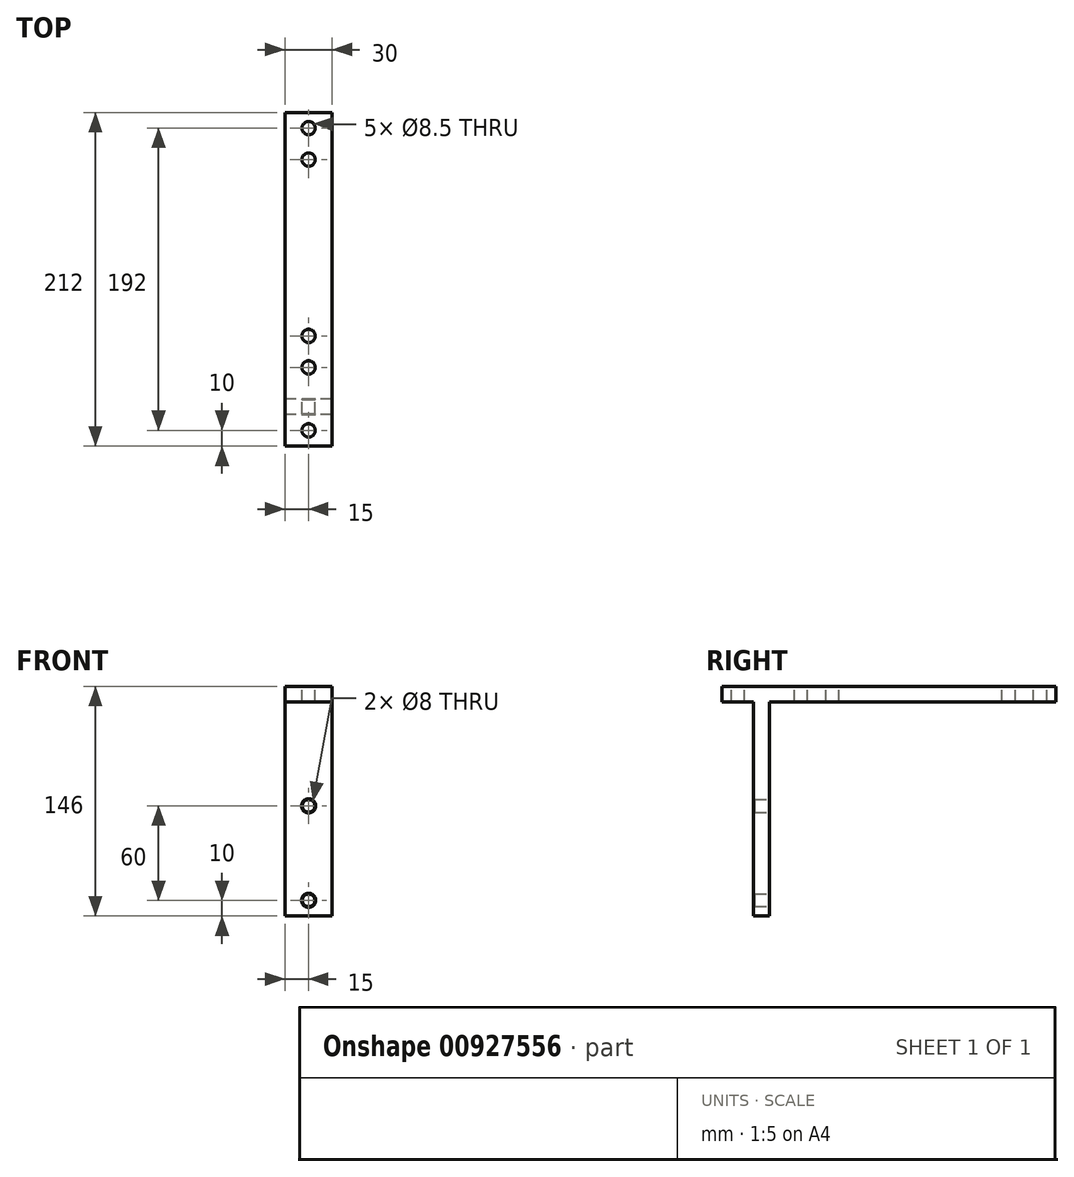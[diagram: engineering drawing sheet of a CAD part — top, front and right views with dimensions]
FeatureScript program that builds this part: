
annotation { "Feature Type Name" : "Feature", "Feature Type Description" : "" }
export const myFeature = defineFeature(function(context is Context, id is Id, definition is map)
    precondition{}
    {
        {
            var Q0;
            Q0=qCreatedBy(makeId("Right.planeOp"),FACE);
            var sketch = newSketch(context, id + "F0", { "sketchPlane" : qUnion([Q0])});
            skLineSegment(sketch, "E0", {"start": v(10, 136) * mm, "end": v(192, 136) * mm});
            skLineSegment(sketch, "E1", {"start": v(10, 136) * mm, "end": v(10, 0) * mm});
            skLineSegment(sketch, "E2.0", {"start": v(0, 146) * mm, "end": v(192, 146) * mm});
            skLineSegment(sketch, "E3.0", {"start": v(0, 136) * mm, "end": v(0, 0) * mm});
            skLineSegment(sketch, "E4", {"start": v(192, 146) * mm, "end": v(192, 136) * mm});
            skLineSegment(sketch, "E5", {"start": v(0, 0) * mm, "end": v(10, 0) * mm});
            skLineSegment(sketch, "E6", {"start": v(0, 146) * mm, "end": v(-20, 146) * mm});
            skLineSegment(sketch, "E7", {"start": v(-20, 146) * mm, "end": v(-20, 136) * mm});
            skLineSegment(sketch, "E8", {"start": v(-20, 136) * mm, "end": v(0, 136) * mm});
            skSolve(sketch);
        }
        {
            var Q0;
            Q0 = qSketchRegion(id + "F0", true);
            extrude(context, id + "F1", {"entities" : qUnion([Q0]), "depth" : 30 * mm, "offsetDistance" : 25 * mm});
        }
        {
            var Q0;
            Q0=makeQuery(id+"F1.opExtrude","SWEPT_FACE",FACE,{"disambiguationData":[OSD([sQuery(id+"F0.wireOp",EDGE,"E1")])]});
            var sketch = newSketch(context, id + "F2", { "sketchPlane" : qUnion([Q0])});
            skLineSegment(sketch, "E9", {"start": v(-15, -28.87) * mm, "end": v(-15, 139.83) * mm, "construction": true});
            skPoint(sketch, "E9.startSnap0", {"position": v(-15, 0) * mm});
            skPoint(sketch, "E9.endSnap0", {"position": v(-15, 136) * mm});
            skCircle(sketch, "E10", {"center": v(-15, 10) * mm, "radius": 4 * mm});
            skCircle(sketch, "E11", {"center": v(-15, 70) * mm, "radius": 4 * mm});
            skSolve(sketch);
        }
        {
            var Q0;
            Q0=makeQuery(id+"F2.imprint","IMPRINT",FACE,{"disambiguationData":[TD([[makeQuery(id+"F2.imprint","IMPRINT",EDGE,{"derivedFrom":sQuery(id+"F2.wireOp",EDGE,"E11")}),1.0]])]});
            var Q1;
            Q1=makeQuery(id+"F2.imprint","IMPRINT",FACE,{"disambiguationData":[TD([[makeQuery(id+"F2.imprint","IMPRINT",EDGE,{"derivedFrom":sQuery(id+"F2.wireOp",EDGE,"E10")}),1.0]])]});
            extrude(context, id + "F3", {"entities" : qUnion([Q0, Q1]), "operationType" : NewBodyOperationType.REMOVE, "endBound" : BoundingType.THROUGH_ALL, "oppositeDirection" : true, "depth" : 25 * mm, "offsetDistance" : 25 * mm});
        }
        {
            var Q0;
            Q0=makeQuery(id+"F3.boolean.opBoolean","COPY",FACE,{"derivedFrom":makeQuery(id+"F3.opExtrude","SWEPT_FACE",FACE,{"disambiguationData":[OSD([sQuery(id+"F2.wireOp",EDGE,"E11")])]})});
            var Q1;
            Q1=makeQuery(id+"F3.boolean.opBoolean","COPY",FACE,{"derivedFrom":makeQuery(id+"F3.opExtrude","SWEPT_FACE",FACE,{"disambiguationData":[OSD([sQuery(id+"F2.wireOp",EDGE,"E10")])]})});
            chamfer(context, id + "F4", {"entities" : qUnion([Q0, Q1]), "width" : 0.5 * mm, "tangentPropagation" : true});
        }
        {
            var Q0;
            Q0=makeQuery(id+"F1.opExtrude","SWEPT_FACE",FACE,{"disambiguationData":[OSD([sQuery(id+"F0.wireOp",EDGE,"E2.0"),sQuery(id+"F0.wireOp",EDGE,"E6")])]});
            var sketch = newSketch(context, id + "F5", { "sketchPlane" : qUnion([Q0])});
            skLineSegment(sketch, "E12", {"start": v(15, 190.85) * mm, "end": v(15, -32.8) * mm, "construction": true});
            skPoint(sketch, "E12.startSnap0", {"position": v(15, 192) * mm});
            skCircle(sketch, "E13", {"center": v(15, 182) * mm, "radius": 4.25 * mm});
            skCircle(sketch, "E14", {"center": v(15, 162) * mm, "radius": 4.25 * mm});
            skCircle(sketch, "E15", {"center": v(15, -10) * mm, "radius": 4.25 * mm});
            skCircle(sketch, "E16", {"center": v(15, 30) * mm, "radius": 4.25 * mm});
            skCircle(sketch, "E17", {"center": v(15, 50) * mm, "radius": 4.25 * mm});
            skSolve(sketch);
        }
        {
            var Q0;
            Q0 = qSketchRegion(id + "F5", true);
            extrude(context, id + "F6", {"entities" : qUnion([Q0]), "operationType" : NewBodyOperationType.REMOVE, "endBound" : BoundingType.THROUGH_ALL, "oppositeDirection" : true, "depth" : 25 * mm, "offsetDistance" : 25 * mm});
        }
    });
